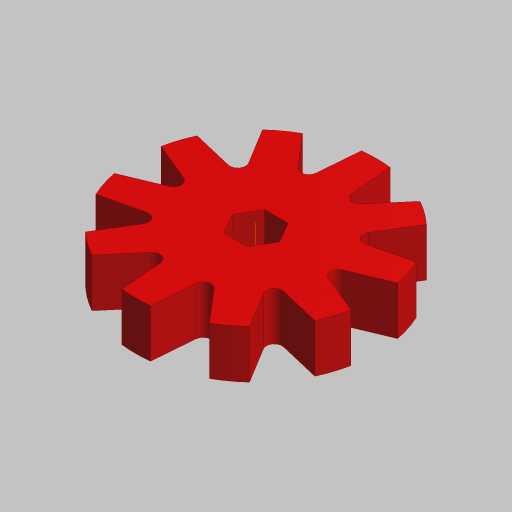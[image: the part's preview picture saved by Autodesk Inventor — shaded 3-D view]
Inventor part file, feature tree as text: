
AUTODESK INVENTOR PART (.ipt)
format: ipt  version: 2023.5 (Build 275446000, 446)  size: 143,360 bytes
history: native  units: mm (DEFAULTED — no unit token found)
features: extrude x1, sketch x1, other x1
ambient origin geometry x8: Origin, YZ Plane, XZ Plane, XY Plane, X Axis, Y Axis, Z Axis, Center Point
bodies: Solid1 (feature_tree)
feature tree (3):
  extrude  "Extrusion1"  TaperAngle=0.0deg  [1 undecoded]
  sketch  "Sketch1"  dims[d0=63.5mm d1=0.0mm d2=0.0mm]
  other  "Cut-Extrude1"
note: 1 required parameter value undecoded (feature->parameter linkage not recoverable at this tier; creation-order binding heuristic only, values carry confidence <= 0.55)
